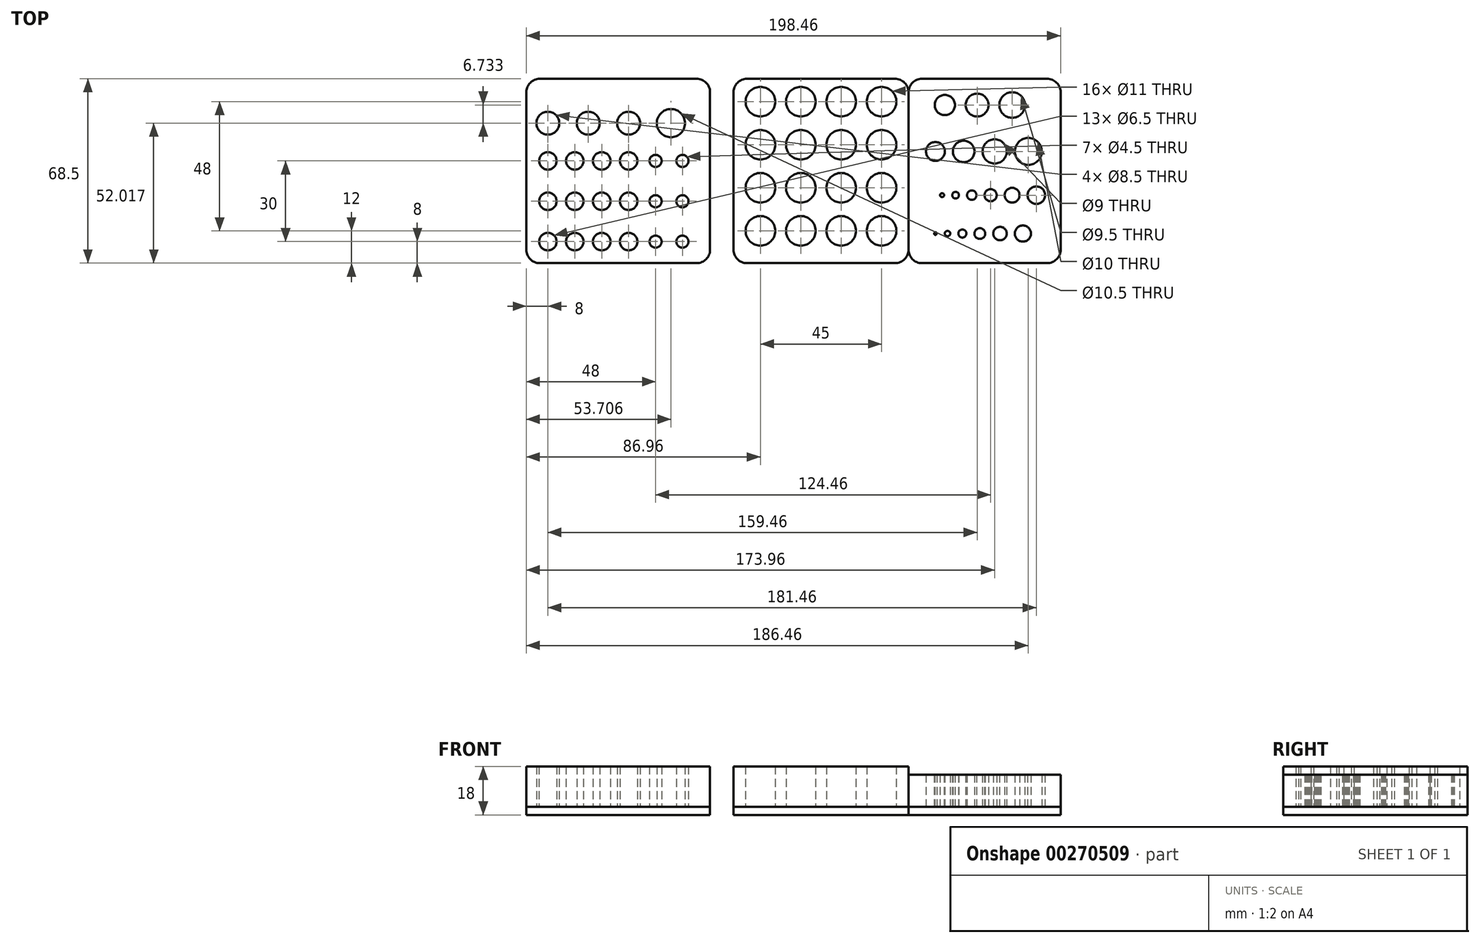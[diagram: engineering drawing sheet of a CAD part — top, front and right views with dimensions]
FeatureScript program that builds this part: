
annotation { "Feature Type Name" : "Feature", "Feature Type Description" : "" }
export const myFeature = defineFeature(function(context is Context, id is Id, definition is map)
    precondition{}
    {
        {
            var Q0;
            Q0=qCreatedBy(makeId("Top.planeOp"),FACE);
            var sketch = newSketch(context, id + "F0", { "sketchPlane" : qUnion([Q0])});
            skLineSegment(sketch, "E0", {"start": v(-11.7, 11) * mm, "end": v(59.1, 11) * mm, "construction": true});
            skCircle(sketch, "E1", {"center": v(10, 11) * mm, "radius": 0.5 * mm});
            skCircle(sketch, "E2", {"center": v(14.5, 11) * mm, "radius": 1 * mm});
            skCircle(sketch, "E3", {"center": v(20, 11) * mm, "radius": 1.5 * mm});
            skCircle(sketch, "E4", {"center": v(26.5, 11) * mm, "radius": 2 * mm});
            skCircle(sketch, "E5", {"center": v(34, 11) * mm, "radius": 2.5 * mm});
            skLineSegment(sketch, "E6", {"start": v(65.12, 25.25) * mm, "end": v(-13.72, 25.25) * mm, "construction": true});
            skCircle(sketch, "E7", {"center": v(12.5, 25.25) * mm, "radius": 0.75 * mm});
            skCircle(sketch, "E8", {"center": v(17.5, 25.25) * mm, "radius": 1.25 * mm});
            skCircle(sketch, "E9", {"center": v(23.5, 25.25) * mm, "radius": 1.75 * mm});
            skCircle(sketch, "E10", {"center": v(30.5, 25.25) * mm, "radius": 2.25 * mm});
            skCircle(sketch, "E11", {"center": v(38.5, 25.25) * mm, "radius": 2.75 * mm});
            skLineSegment(sketch, "E12", {"start": v(-11.82, 41.5) * mm, "end": v(56.53, 41.5) * mm, "construction": true});
            skCircle(sketch, "E13", {"center": v(42.5, 11) * mm, "radius": 3 * mm});
            skCircle(sketch, "E14", {"center": v(47.5, 25.25) * mm, "radius": 3.25 * mm});
            skCircle(sketch, "E15", {"center": v(10, 41.5) * mm, "radius": 3.5 * mm});
            skCircle(sketch, "E16", {"center": v(20.5, 41.5) * mm, "radius": 4 * mm});
            skCircle(sketch, "E17", {"center": v(32, 41.5) * mm, "radius": 4.5 * mm});
            skLineSegment(sketch, "E18", {"start": v(-15.7, 58.75) * mm, "end": v(58.24, 58.75) * mm, "construction": true});
            skCircle(sketch, "E19", {"center": v(13.5, 58.75) * mm, "radius": 3.75 * mm});
            skCircle(sketch, "E20", {"center": v(25.5, 58.75) * mm, "radius": 4.25 * mm});
            skCircle(sketch, "E21", {"center": v(38.5, 58.75) * mm, "radius": 4.75 * mm});
            skCircle(sketch, "E22", {"center": v(44.5, 41.5) * mm, "radius": 5 * mm});
            skLineSegment(sketch, "E23.bottom", {"start": v(5, 68.5) * mm, "end": v(51.5, 68.5) * mm});
            skLineSegment(sketch, "E23.top", {"start": v(5, 0) * mm, "end": v(51.5, 0) * mm});
            skLineSegment(sketch, "E23.left", {"start": v(0, 63.5) * mm, "end": v(0, 5) * mm});
            skLineSegment(sketch, "E23.right", {"start": v(56.5, 63.5) * mm, "end": v(56.5, 5) * mm});
            skPoint(sketch, "E24.visualSharp", {"position": v(0, 68.5) * mm});
            skArc(sketch, "E24.filletArc", {"start": v(5, 68.5) * mm, "mid": v(1.46, 67.04) * mm, "end": v(0, 63.5) * mm});
            skPoint(sketch, "E25.visualSharp", {"position": v(56.5, 68.5) * mm});
            skArc(sketch, "E25.filletArc", {"start": v(56.5, 63.5) * mm, "mid": v(55.04, 67.04) * mm, "end": v(51.5, 68.5) * mm});
            skPoint(sketch, "E26.visualSharp", {"position": v(56.5, 0) * mm});
            skArc(sketch, "E26.filletArc", {"start": v(51.5, 0) * mm, "mid": v(55.04, 1.46) * mm, "end": v(56.5, 5) * mm});
            skPoint(sketch, "E27.visualSharp", {"position": v(0, 0) * mm});
            skArc(sketch, "E27.filletArc", {"start": v(0, 5) * mm, "mid": v(1.46, 1.46) * mm, "end": v(5, 0) * mm});
            skSolve(sketch);
        }
        {
            var Q0;
            Q0=makeQuery(id+"F0.imprint","IMPRINT",FACE,{"disambiguationData":[TD([[makeQuery(id+"F0.imprint","IMPRINT",EDGE,{"derivedFrom":sQuery(id+"F0.wireOp",EDGE,"E1")}),-1.0]])]});
            extrude(context, id + "F1", {"entities" : qUnion([Q0]), "depth" : 3 * 4 * mm});
        }
        {
            var Q0;
            Q0=makeQuery(id+"F0.imprint","IMPRINT",FACE,{"disambiguationData":[TD([[makeQuery(id+"F0.imprint","IMPRINT",EDGE,{"derivedFrom":sQuery(id+"F0.wireOp",EDGE,"E19")}),1.0]])]});
            var Q1;
            Q1=makeQuery(id+"F0.imprint","IMPRINT",FACE,{"disambiguationData":[TD([[makeQuery(id+"F0.imprint","IMPRINT",EDGE,{"derivedFrom":sQuery(id+"F0.wireOp",EDGE,"E20")}),1.0]])]});
            var Q2;
            Q2=makeQuery(id+"F0.imprint","IMPRINT",FACE,{"disambiguationData":[TD([[makeQuery(id+"F0.imprint","IMPRINT",EDGE,{"derivedFrom":sQuery(id+"F0.wireOp",EDGE,"E21")}),1.0]])]});
            var Q3;
            Q3=makeQuery(id+"F0.imprint","IMPRINT",FACE,{"disambiguationData":[TD([[makeQuery(id+"F0.imprint","IMPRINT",EDGE,{"derivedFrom":sQuery(id+"F0.wireOp",EDGE,"E22")}),1.0]])]});
            var Q4;
            Q4=makeQuery(id+"F0.imprint","IMPRINT",FACE,{"disambiguationData":[TD([[makeQuery(id+"F0.imprint","IMPRINT",EDGE,{"derivedFrom":sQuery(id+"F0.wireOp",EDGE,"E17")}),1.0]])]});
            var Q5;
            Q5=makeQuery(id+"F0.imprint","IMPRINT",FACE,{"disambiguationData":[TD([[makeQuery(id+"F0.imprint","IMPRINT",EDGE,{"derivedFrom":sQuery(id+"F0.wireOp",EDGE,"E16")}),1.0]])]});
            var Q6;
            Q6=makeQuery(id+"F0.imprint","IMPRINT",FACE,{"disambiguationData":[TD([[makeQuery(id+"F0.imprint","IMPRINT",EDGE,{"derivedFrom":sQuery(id+"F0.wireOp",EDGE,"E15")}),1.0]])]});
            var Q7;
            Q7=makeQuery(id+"F0.imprint","IMPRINT",FACE,{"disambiguationData":[TD([[makeQuery(id+"F0.imprint","IMPRINT",EDGE,{"derivedFrom":sQuery(id+"F0.wireOp",EDGE,"E7")}),1.0]])]});
            var Q8;
            Q8=makeQuery(id+"F0.imprint","IMPRINT",FACE,{"disambiguationData":[TD([[makeQuery(id+"F0.imprint","IMPRINT",EDGE,{"derivedFrom":sQuery(id+"F0.wireOp",EDGE,"E8")}),1.0]])]});
            var Q9;
            Q9=makeQuery(id+"F0.imprint","IMPRINT",FACE,{"disambiguationData":[TD([[makeQuery(id+"F0.imprint","IMPRINT",EDGE,{"derivedFrom":sQuery(id+"F0.wireOp",EDGE,"E9")}),1.0]])]});
            var Q10;
            Q10=makeQuery(id+"F0.imprint","IMPRINT",FACE,{"disambiguationData":[TD([[makeQuery(id+"F0.imprint","IMPRINT",EDGE,{"derivedFrom":sQuery(id+"F0.wireOp",EDGE,"E10")}),1.0]])]});
            var Q11;
            Q11=makeQuery(id+"F0.imprint","IMPRINT",FACE,{"disambiguationData":[TD([[makeQuery(id+"F0.imprint","IMPRINT",EDGE,{"derivedFrom":sQuery(id+"F0.wireOp",EDGE,"E11")}),1.0]])]});
            var Q12;
            Q12=makeQuery(id+"F0.imprint","IMPRINT",FACE,{"disambiguationData":[TD([[makeQuery(id+"F0.imprint","IMPRINT",EDGE,{"derivedFrom":sQuery(id+"F0.wireOp",EDGE,"E14")}),1.0]])]});
            var Q13;
            Q13=makeQuery(id+"F0.imprint","IMPRINT",FACE,{"disambiguationData":[TD([[makeQuery(id+"F0.imprint","IMPRINT",EDGE,{"derivedFrom":sQuery(id+"F0.wireOp",EDGE,"E13")}),1.0]])]});
            var Q14;
            Q14=makeQuery(id+"F0.imprint","IMPRINT",FACE,{"disambiguationData":[TD([[makeQuery(id+"F0.imprint","IMPRINT",EDGE,{"derivedFrom":sQuery(id+"F0.wireOp",EDGE,"E5")}),1.0]])]});
            var Q15;
            Q15=makeQuery(id+"F0.imprint","IMPRINT",FACE,{"disambiguationData":[TD([[makeQuery(id+"F0.imprint","IMPRINT",EDGE,{"derivedFrom":sQuery(id+"F0.wireOp",EDGE,"E4")}),1.0]])]});
            var Q16;
            Q16=makeQuery(id+"F0.imprint","IMPRINT",FACE,{"disambiguationData":[TD([[makeQuery(id+"F0.imprint","IMPRINT",EDGE,{"derivedFrom":sQuery(id+"F0.wireOp",EDGE,"E3")}),1.0]])]});
            var Q17;
            Q17=makeQuery(id+"F0.imprint","IMPRINT",FACE,{"disambiguationData":[TD([[makeQuery(id+"F0.imprint","IMPRINT",EDGE,{"derivedFrom":sQuery(id+"F0.wireOp",EDGE,"E2")}),1.0]])]});
            var Q18;
            Q18=makeQuery(id+"F0.imprint","IMPRINT",FACE,{"disambiguationData":[TD([[makeQuery(id+"F0.imprint","IMPRINT",EDGE,{"derivedFrom":sQuery(id+"F0.wireOp",EDGE,"E1")}),-1.0]])]});
            var Q19;
            Q19=makeQuery(id+"F0.imprint","IMPRINT",FACE,{"disambiguationData":[TD([[makeQuery(id+"F0.imprint","IMPRINT",EDGE,{"derivedFrom":sQuery(id+"F0.wireOp",EDGE,"E1")}),1.0]])]});
            extrude(context, id + "F2", {"entities" : qUnion([Q0, Q1, Q2, Q3, Q4, Q5, Q6, Q7, Q8, Q9, Q10, Q11, Q12, Q13, Q14, Q15, Q16, Q17, Q18, Q19]), "oppositeDirection" : true, "depth" : 3 * mm});
        }
        {
            var Q0;
            Q0=qCreatedBy(makeId("Top.planeOp"),FACE);
            var sketch = newSketch(context, id + "F3", { "sketchPlane" : qUnion([Q0])});
            skLineSegment(sketch, "E28.bottom", {"start": v(-5, 0) * mm, "end": v(-60, 0) * mm});
            skLineSegment(sketch, "E28.top", {"start": v(-5, 68.5) * mm, "end": v(-60, 68.5) * mm});
            skLineSegment(sketch, "E28.left", {"start": v(0, 5) * mm, "end": v(0, 63.5) * mm});
            skLineSegment(sketch, "E28.right", {"start": v(-65, 5) * mm, "end": v(-65, 63.5) * mm});
            skCircle(sketch, "E29", {"center": v(-55, 12) * mm, "radius": 5.5 * mm});
            skCircle(sketch, "E30.1.0.0", {"center": v(-40, 12) * mm, "radius": 5.5 * mm});
            skCircle(sketch, "E30.2.0.0", {"center": v(-25, 12) * mm, "radius": 5.5 * mm});
            skCircle(sketch, "E30.3.0.0", {"center": v(-10, 12) * mm, "radius": 5.5 * mm});
            skLineSegment(sketch, "E30.direction1", {"start": v(-55, 12) * mm, "end": v(-40, 12) * mm, "construction": true});
            skLineSegment(sketch, "E30.direction2", {"start": v(-55, 12) * mm, "end": v(-55, 28) * mm, "construction": true});
            skCircle(sketch, "E31.0.0.1", {"center": v(-55, 28) * mm, "radius": 5.5 * mm});
            skCircle(sketch, "E31.0.0.2", {"center": v(-55, 44) * mm, "radius": 5.5 * mm});
            skCircle(sketch, "E31.0.0.3", {"center": v(-55, 60) * mm, "radius": 5.5 * mm});
            skCircle(sketch, "E31.0.1.1", {"center": v(-40, 28) * mm, "radius": 5.5 * mm});
            skCircle(sketch, "E31.0.1.2", {"center": v(-40, 44) * mm, "radius": 5.5 * mm});
            skCircle(sketch, "E31.0.1.3", {"center": v(-40, 60) * mm, "radius": 5.5 * mm});
            skCircle(sketch, "E31.0.2.1", {"center": v(-25, 28) * mm, "radius": 5.5 * mm});
            skCircle(sketch, "E31.0.2.2", {"center": v(-25, 44) * mm, "radius": 5.5 * mm});
            skCircle(sketch, "E31.0.2.3", {"center": v(-25, 60) * mm, "radius": 5.5 * mm});
            skCircle(sketch, "E31.0.3.1", {"center": v(-10, 28) * mm, "radius": 5.5 * mm});
            skCircle(sketch, "E31.0.3.2", {"center": v(-10, 44) * mm, "radius": 5.5 * mm});
            skCircle(sketch, "E31.0.3.3", {"center": v(-10, 60) * mm, "radius": 5.5 * mm});
            skPoint(sketch, "E32.visualSharp", {"position": v(-65, 68.5) * mm});
            skArc(sketch, "E32.filletArc", {"start": v(-60, 68.5) * mm, "mid": v(-63.54, 67.04) * mm, "end": v(-65, 63.5) * mm});
            skPoint(sketch, "E33.visualSharp", {"position": v(0, 68.5) * mm});
            skArc(sketch, "E33.filletArc", {"start": v(0, 63.5) * mm, "mid": v(-1.46, 67.04) * mm, "end": v(-5, 68.5) * mm});
            skPoint(sketch, "E34.visualSharp", {"position": v(0, 0) * mm});
            skArc(sketch, "E34.filletArc", {"start": v(-5, 0) * mm, "mid": v(-1.46, 1.46) * mm, "end": v(0, 5) * mm});
            skPoint(sketch, "E35.visualSharp", {"position": v(-65, 0) * mm});
            skArc(sketch, "E35.filletArc", {"start": v(-65, 5) * mm, "mid": v(-63.54, 1.46) * mm, "end": v(-60, 0) * mm});
            skSolve(sketch);
        }
        {
            var Q0;
            Q0=makeQuery(id+"F3.imprint","IMPRINT",FACE,{"disambiguationData":[TD([[makeQuery(id+"F3.imprint","IMPRINT",EDGE,{"derivedFrom":sQuery(id+"F3.wireOp",EDGE,"E28.bottom")}),-1.0]])]});
            extrude(context, id + "F4", {"entities" : qUnion([Q0]), "depth" : 15 * mm});
        }
        {
            var Q0;
            Q0=makeQuery(id+"F3.imprint","IMPRINT",FACE,{"disambiguationData":[TD([[makeQuery(id+"F3.imprint","IMPRINT",EDGE,{"derivedFrom":sQuery(id+"F3.wireOp",EDGE,"E28.bottom")}),-1.0]])]});
            var Q1;
            Q1=makeQuery(id+"F3.imprint","IMPRINT",FACE,{"disambiguationData":[TD([[makeQuery(id+"F3.imprint","IMPRINT",EDGE,{"derivedFrom":sQuery(id+"F3.wireOp",EDGE,"E29")}),1.0]])]});
            var Q2;
            Q2=makeQuery(id+"F3.imprint","IMPRINT",FACE,{"disambiguationData":[TD([[makeQuery(id+"F3.imprint","IMPRINT",EDGE,{"derivedFrom":sQuery(id+"F3.wireOp",EDGE,"E31.0.0.1")}),1.0]])]});
            var Q3;
            Q3=makeQuery(id+"F3.imprint","IMPRINT",FACE,{"disambiguationData":[TD([[makeQuery(id+"F3.imprint","IMPRINT",EDGE,{"derivedFrom":sQuery(id+"F3.wireOp",EDGE,"E31.0.0.2")}),1.0]])]});
            var Q4;
            Q4=makeQuery(id+"F3.imprint","IMPRINT",FACE,{"disambiguationData":[TD([[makeQuery(id+"F3.imprint","IMPRINT",EDGE,{"derivedFrom":sQuery(id+"F3.wireOp",EDGE,"E31.0.0.3")}),1.0]])]});
            var Q5;
            Q5=makeQuery(id+"F3.imprint","IMPRINT",FACE,{"disambiguationData":[TD([[makeQuery(id+"F3.imprint","IMPRINT",EDGE,{"derivedFrom":sQuery(id+"F3.wireOp",EDGE,"E31.0.1.3")}),1.0]])]});
            var Q6;
            Q6=makeQuery(id+"F3.imprint","IMPRINT",FACE,{"disambiguationData":[TD([[makeQuery(id+"F3.imprint","IMPRINT",EDGE,{"derivedFrom":sQuery(id+"F3.wireOp",EDGE,"E31.0.1.2")}),1.0]])]});
            var Q7;
            Q7=makeQuery(id+"F3.imprint","IMPRINT",FACE,{"disambiguationData":[TD([[makeQuery(id+"F3.imprint","IMPRINT",EDGE,{"derivedFrom":sQuery(id+"F3.wireOp",EDGE,"E31.0.1.1")}),1.0]])]});
            var Q8;
            Q8=makeQuery(id+"F3.imprint","IMPRINT",FACE,{"disambiguationData":[TD([[makeQuery(id+"F3.imprint","IMPRINT",EDGE,{"derivedFrom":sQuery(id+"F3.wireOp",EDGE,"E30.1.0.0")}),1.0]])]});
            var Q9;
            Q9=makeQuery(id+"F3.imprint","IMPRINT",FACE,{"disambiguationData":[TD([[makeQuery(id+"F3.imprint","IMPRINT",EDGE,{"derivedFrom":sQuery(id+"F3.wireOp",EDGE,"E30.2.0.0")}),1.0]])]});
            var Q10;
            Q10=makeQuery(id+"F3.imprint","IMPRINT",FACE,{"disambiguationData":[TD([[makeQuery(id+"F3.imprint","IMPRINT",EDGE,{"derivedFrom":sQuery(id+"F3.wireOp",EDGE,"E31.0.2.1")}),1.0]])]});
            var Q11;
            Q11=makeQuery(id+"F3.imprint","IMPRINT",FACE,{"disambiguationData":[TD([[makeQuery(id+"F3.imprint","IMPRINT",EDGE,{"derivedFrom":sQuery(id+"F3.wireOp",EDGE,"E31.0.2.2")}),1.0]])]});
            var Q12;
            Q12=makeQuery(id+"F3.imprint","IMPRINT",FACE,{"disambiguationData":[TD([[makeQuery(id+"F3.imprint","IMPRINT",EDGE,{"derivedFrom":sQuery(id+"F3.wireOp",EDGE,"E31.0.2.3")}),1.0]])]});
            var Q13;
            Q13=makeQuery(id+"F3.imprint","IMPRINT",FACE,{"disambiguationData":[TD([[makeQuery(id+"F3.imprint","IMPRINT",EDGE,{"derivedFrom":sQuery(id+"F3.wireOp",EDGE,"E31.0.3.3")}),1.0]])]});
            var Q14;
            Q14=makeQuery(id+"F3.imprint","IMPRINT",FACE,{"disambiguationData":[TD([[makeQuery(id+"F3.imprint","IMPRINT",EDGE,{"derivedFrom":sQuery(id+"F3.wireOp",EDGE,"E31.0.3.2")}),1.0]])]});
            var Q15;
            Q15=makeQuery(id+"F3.imprint","IMPRINT",FACE,{"disambiguationData":[TD([[makeQuery(id+"F3.imprint","IMPRINT",EDGE,{"derivedFrom":sQuery(id+"F3.wireOp",EDGE,"E31.0.3.1")}),1.0]])]});
            var Q16;
            Q16=makeQuery(id+"F3.imprint","IMPRINT",FACE,{"disambiguationData":[TD([[makeQuery(id+"F3.imprint","IMPRINT",EDGE,{"derivedFrom":sQuery(id+"F3.wireOp",EDGE,"E30.3.0.0")}),1.0]])]});
            extrude(context, id + "F5", {"entities" : qUnion([Q0, Q1, Q2, Q3, Q4, Q5, Q6, Q7, Q8, Q9, Q10, Q11, Q12, Q13, Q14, Q15, Q16]), "oppositeDirection" : true, "depth" : 3 * mm});
        }
        {
            var Q0;
            Q0=qCreatedBy(makeId("Top.planeOp"),FACE);
            var sketch = newSketch(context, id + "F6", { "sketchPlane" : qUnion([Q0])});
            skLineSegment(sketch, "E36.bottom", {"start": v(-78.7, 0) * mm, "end": v(-136.96, 0) * mm});
            skLineSegment(sketch, "E36.top", {"start": v(-78.7, 68.5) * mm, "end": v(-136.96, 68.5) * mm});
            skLineSegment(sketch, "E36.left", {"start": v(-73.7, 5) * mm, "end": v(-73.7, 63.5) * mm});
            skLineSegment(sketch, "E36.right", {"start": v(-141.96, 5) * mm, "end": v(-141.96, 63.5) * mm});
            skCircle(sketch, "E37", {"center": v(-133.96, 8) * mm, "radius": 3.25 * mm});
            skCircle(sketch, "E38.0.1.0", {"center": v(-133.96, 23) * mm, "radius": 3.25 * mm});
            skCircle(sketch, "E38.0.2.0", {"center": v(-133.96, 38) * mm, "radius": 3.25 * mm});
            skCircle(sketch, "E38.1.0.0", {"center": v(-123.96, 8) * mm, "radius": 3.25 * mm});
            skCircle(sketch, "E38.1.1.0", {"center": v(-123.96, 23) * mm, "radius": 3.25 * mm});
            skCircle(sketch, "E38.1.2.0", {"center": v(-123.96, 38) * mm, "radius": 3.25 * mm});
            skCircle(sketch, "E38.2.0.0", {"center": v(-113.96, 8) * mm, "radius": 3.25 * mm});
            skCircle(sketch, "E38.2.1.0", {"center": v(-113.96, 23) * mm, "radius": 3.25 * mm});
            skCircle(sketch, "E38.2.2.0", {"center": v(-113.96, 38) * mm, "radius": 3.25 * mm});
            skCircle(sketch, "E38.3.0.0", {"center": v(-103.96, 8) * mm, "radius": 3.25 * mm});
            skCircle(sketch, "E38.3.1.0", {"center": v(-103.96, 23) * mm, "radius": 3.25 * mm});
            skCircle(sketch, "E38.3.2.0", {"center": v(-103.96, 38) * mm, "radius": 3.25 * mm});
            skLineSegment(sketch, "E38.direction1", {"start": v(-133.96, 8) * mm, "end": v(-123.96, 8) * mm, "construction": true});
            skLineSegment(sketch, "E38.direction2", {"start": v(-133.96, 8) * mm, "end": v(-133.96, 23) * mm, "construction": true});
            skCircle(sketch, "E39", {"center": v(-133.96, 52.02) * mm, "radius": 4.25 * mm});
            skCircle(sketch, "E40", {"center": v(-93.96, 8) * mm, "radius": 2.25 * mm});
            skCircle(sketch, "E41.0.1.0", {"center": v(-93.96, 23) * mm, "radius": 2.25 * mm});
            skCircle(sketch, "E41.0.2.0", {"center": v(-93.96, 38) * mm, "radius": 2.25 * mm});
            skCircle(sketch, "E41.1.0.0", {"center": v(-83.96, 8) * mm, "radius": 2.25 * mm});
            skCircle(sketch, "E41.1.1.0", {"center": v(-83.96, 23) * mm, "radius": 2.25 * mm});
            skCircle(sketch, "E41.1.2.0", {"center": v(-83.96, 38) * mm, "radius": 2.25 * mm});
            skLineSegment(sketch, "E41.direction1", {"start": v(-93.96, 8) * mm, "end": v(-83.96, 8) * mm, "construction": true});
            skLineSegment(sketch, "E41.direction2", {"start": v(-93.96, 8) * mm, "end": v(-93.96, 23) * mm, "construction": true});
            skCircle(sketch, "E42.1.0.0", {"center": v(-118.96, 52.02) * mm, "radius": 4.25 * mm});
            skCircle(sketch, "E42.2.0.0", {"center": v(-103.96, 52.02) * mm, "radius": 4.25 * mm});
            skLineSegment(sketch, "E42.direction1", {"start": v(-133.96, 52.02) * mm, "end": v(-118.96, 52.02) * mm, "construction": true});
            skCircle(sketch, "E43", {"center": v(-88.25, 52.02) * mm, "radius": 5.25 * mm});
            skPoint(sketch, "E44.visualSharp", {"position": v(-141.96, 68.5) * mm});
            skArc(sketch, "E44.filletArc", {"start": v(-136.96, 68.5) * mm, "mid": v(-140.5, 67.04) * mm, "end": v(-141.96, 63.5) * mm});
            skPoint(sketch, "E45.visualSharp", {"position": v(-73.7, 68.5) * mm});
            skArc(sketch, "E45.filletArc", {"start": v(-73.7, 63.5) * mm, "mid": v(-75.17, 67.04) * mm, "end": v(-78.7, 68.5) * mm});
            skPoint(sketch, "E46.visualSharp", {"position": v(-73.7, 0) * mm});
            skArc(sketch, "E46.filletArc", {"start": v(-78.7, 0) * mm, "mid": v(-75.17, 1.46) * mm, "end": v(-73.7, 5) * mm});
            skPoint(sketch, "E47.visualSharp", {"position": v(-141.96, 0) * mm});
            skArc(sketch, "E47.filletArc", {"start": v(-141.96, 5) * mm, "mid": v(-140.5, 1.46) * mm, "end": v(-136.96, 0) * mm});
            skSolve(sketch);
        }
        {
            var Q0;
            Q0=makeQuery(id+"F6.imprint","IMPRINT",FACE,{"disambiguationData":[TD([[makeQuery(id+"F6.imprint","IMPRINT",EDGE,{"derivedFrom":sQuery(id+"F6.wireOp",EDGE,"E36.bottom")}),-1.0]])]});
            extrude(context, id + "F7", {"entities" : qUnion([Q0]), "depth" : 15 * mm});
        }
        {
            var Q0;
            Q0=makeQuery(id+"F6.imprint","IMPRINT",FACE,{"disambiguationData":[TD([[makeQuery(id+"F6.imprint","IMPRINT",EDGE,{"derivedFrom":sQuery(id+"F6.wireOp",EDGE,"E39")}),1.0]])]});
            var Q1;
            Q1=makeQuery(id+"F6.imprint","IMPRINT",FACE,{"disambiguationData":[TD([[makeQuery(id+"F6.imprint","IMPRINT",EDGE,{"derivedFrom":sQuery(id+"F6.wireOp",EDGE,"E42.1.0.0")}),1.0]])]});
            var Q2;
            Q2=makeQuery(id+"F6.imprint","IMPRINT",FACE,{"disambiguationData":[TD([[makeQuery(id+"F6.imprint","IMPRINT",EDGE,{"derivedFrom":sQuery(id+"F6.wireOp",EDGE,"E42.2.0.0")}),1.0]])]});
            var Q3;
            Q3=makeQuery(id+"F6.imprint","IMPRINT",FACE,{"disambiguationData":[TD([[makeQuery(id+"F6.imprint","IMPRINT",EDGE,{"derivedFrom":sQuery(id+"F6.wireOp",EDGE,"E43")}),1.0]])]});
            var Q4;
            Q4=makeQuery(id+"F6.imprint","IMPRINT",FACE,{"disambiguationData":[TD([[makeQuery(id+"F6.imprint","IMPRINT",EDGE,{"derivedFrom":sQuery(id+"F6.wireOp",EDGE,"E41.1.2.0")}),1.0]])]});
            var Q5;
            Q5=makeQuery(id+"F6.imprint","IMPRINT",FACE,{"disambiguationData":[TD([[makeQuery(id+"F6.imprint","IMPRINT",EDGE,{"derivedFrom":sQuery(id+"F6.wireOp",EDGE,"E41.0.2.0")}),1.0]])]});
            var Q6;
            Q6=makeQuery(id+"F6.imprint","IMPRINT",FACE,{"disambiguationData":[TD([[makeQuery(id+"F6.imprint","IMPRINT",EDGE,{"derivedFrom":sQuery(id+"F6.wireOp",EDGE,"E38.3.2.0")}),1.0]])]});
            var Q7;
            Q7=makeQuery(id+"F6.imprint","IMPRINT",FACE,{"disambiguationData":[TD([[makeQuery(id+"F6.imprint","IMPRINT",EDGE,{"derivedFrom":sQuery(id+"F6.wireOp",EDGE,"E38.1.2.0")}),1.0]])]});
            var Q8;
            Q8=makeQuery(id+"F6.imprint","IMPRINT",FACE,{"disambiguationData":[TD([[makeQuery(id+"F6.imprint","IMPRINT",EDGE,{"derivedFrom":sQuery(id+"F6.wireOp",EDGE,"E38.0.2.0")}),1.0]])]});
            var Q9;
            Q9=makeQuery(id+"F6.imprint","IMPRINT",FACE,{"disambiguationData":[TD([[makeQuery(id+"F6.imprint","IMPRINT",EDGE,{"derivedFrom":sQuery(id+"F6.wireOp",EDGE,"E38.0.1.0")}),1.0]])]});
            var Q10;
            Q10=makeQuery(id+"F6.imprint","IMPRINT",FACE,{"disambiguationData":[TD([[makeQuery(id+"F6.imprint","IMPRINT",EDGE,{"derivedFrom":sQuery(id+"F6.wireOp",EDGE,"E38.1.1.0")}),1.0]])]});
            var Q11;
            Q11=makeQuery(id+"F6.imprint","IMPRINT",FACE,{"disambiguationData":[TD([[makeQuery(id+"F6.imprint","IMPRINT",EDGE,{"derivedFrom":sQuery(id+"F6.wireOp",EDGE,"E38.2.1.0")}),1.0]])]});
            var Q12;
            Q12=makeQuery(id+"F6.imprint","IMPRINT",FACE,{"disambiguationData":[TD([[makeQuery(id+"F6.imprint","IMPRINT",EDGE,{"derivedFrom":sQuery(id+"F6.wireOp",EDGE,"E38.3.1.0")}),1.0]])]});
            var Q13;
            Q13=makeQuery(id+"F6.imprint","IMPRINT",FACE,{"disambiguationData":[TD([[makeQuery(id+"F6.imprint","IMPRINT",EDGE,{"derivedFrom":sQuery(id+"F6.wireOp",EDGE,"E41.0.1.0")}),1.0]])]});
            var Q14;
            Q14=makeQuery(id+"F6.imprint","IMPRINT",FACE,{"disambiguationData":[TD([[makeQuery(id+"F6.imprint","IMPRINT",EDGE,{"derivedFrom":sQuery(id+"F6.wireOp",EDGE,"E41.1.1.0")}),1.0]])]});
            var Q15;
            Q15=makeQuery(id+"F6.imprint","IMPRINT",FACE,{"disambiguationData":[TD([[makeQuery(id+"F6.imprint","IMPRINT",EDGE,{"derivedFrom":sQuery(id+"F6.wireOp",EDGE,"E41.1.0.0")}),1.0]])]});
            var Q16;
            Q16=makeQuery(id+"F6.imprint","IMPRINT",FACE,{"disambiguationData":[TD([[makeQuery(id+"F6.imprint","IMPRINT",EDGE,{"derivedFrom":sQuery(id+"F6.wireOp",EDGE,"E40")}),1.0]])]});
            var Q17;
            Q17=makeQuery(id+"F6.imprint","IMPRINT",FACE,{"disambiguationData":[TD([[makeQuery(id+"F6.imprint","IMPRINT",EDGE,{"derivedFrom":sQuery(id+"F6.wireOp",EDGE,"E38.3.0.0")}),1.0]])]});
            var Q18;
            Q18=makeQuery(id+"F6.imprint","IMPRINT",FACE,{"disambiguationData":[TD([[makeQuery(id+"F6.imprint","IMPRINT",EDGE,{"derivedFrom":sQuery(id+"F6.wireOp",EDGE,"E38.2.0.0")}),1.0]])]});
            var Q19;
            Q19=makeQuery(id+"F6.imprint","IMPRINT",FACE,{"disambiguationData":[TD([[makeQuery(id+"F6.imprint","IMPRINT",EDGE,{"derivedFrom":sQuery(id+"F6.wireOp",EDGE,"E38.1.0.0")}),1.0]])]});
            var Q20;
            Q20=makeQuery(id+"F6.imprint","IMPRINT",FACE,{"disambiguationData":[TD([[makeQuery(id+"F6.imprint","IMPRINT",EDGE,{"derivedFrom":sQuery(id+"F6.wireOp",EDGE,"E37")}),1.0]])]});
            var Q21;
            Q21=makeQuery(id+"F6.imprint","IMPRINT",FACE,{"disambiguationData":[TD([[makeQuery(id+"F6.imprint","IMPRINT",EDGE,{"derivedFrom":sQuery(id+"F6.wireOp",EDGE,"E38.2.2.0")}),1.0]])]});
            var Q22;
            Q22=makeQuery(id+"F6.imprint","IMPRINT",FACE,{"disambiguationData":[TD([[makeQuery(id+"F6.imprint","IMPRINT",EDGE,{"derivedFrom":sQuery(id+"F6.wireOp",EDGE,"E36.bottom")}),-1.0]])]});
            extrude(context, id + "F8", {"entities" : qUnion([Q0, Q1, Q2, Q3, Q4, Q5, Q6, Q7, Q8, Q9, Q10, Q11, Q12, Q13, Q14, Q15, Q16, Q17, Q18, Q19, Q20, Q21, Q22]), "oppositeDirection" : true, "depth" : 3 * mm});
        }
    });
